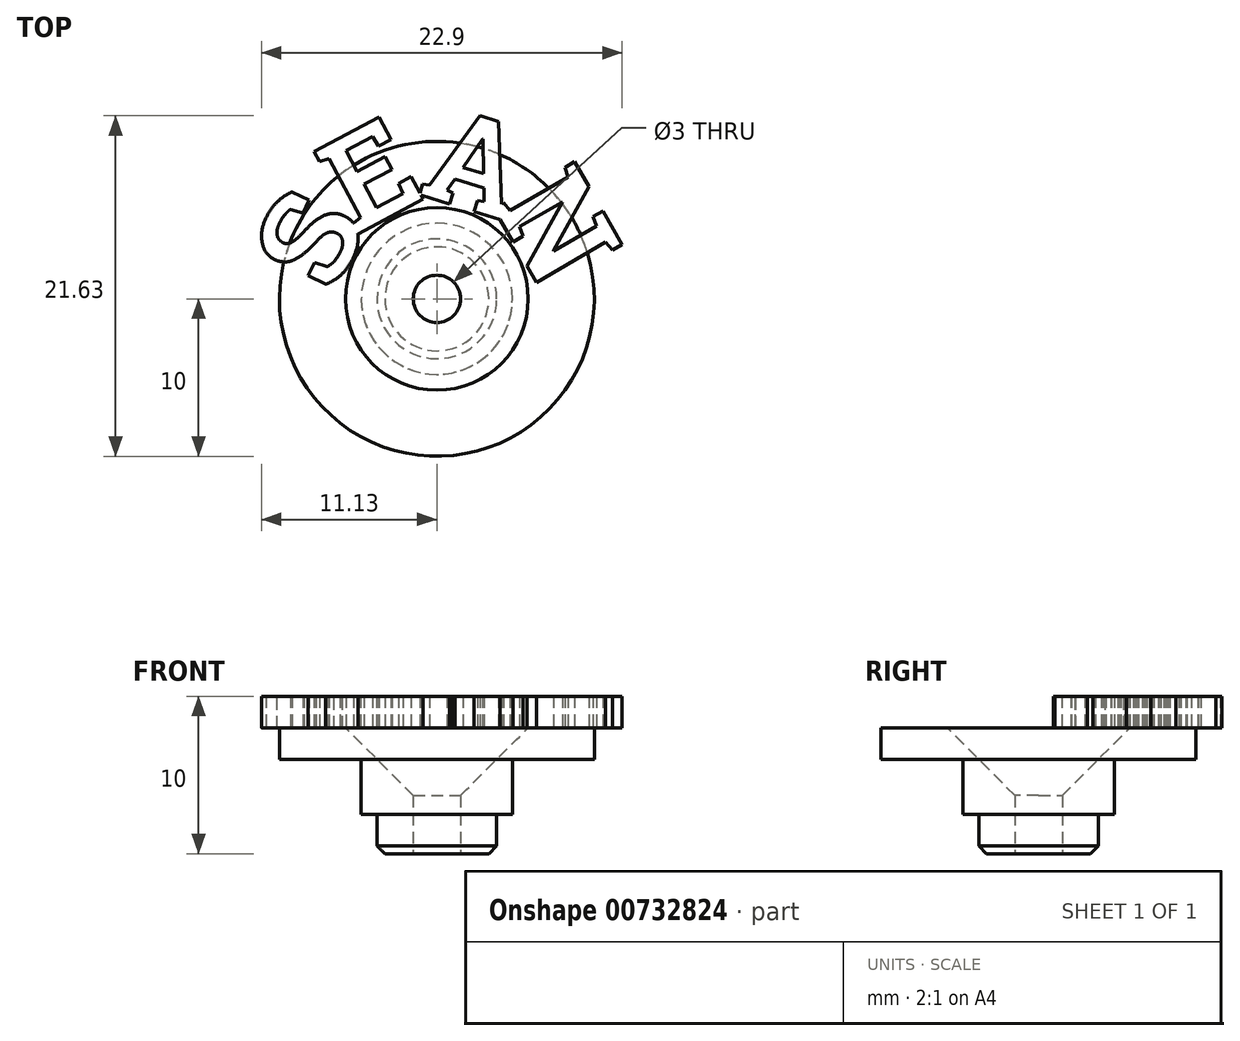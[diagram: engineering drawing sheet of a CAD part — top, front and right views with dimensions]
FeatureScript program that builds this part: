
annotation { "Feature Type Name" : "Feature", "Feature Type Description" : "" }
export const myFeature = defineFeature(function(context is Context, id is Id, definition is map)
    precondition{}
    {
        {
            var Q0;
            Q0=qCreatedBy(makeId("Top.planeOp"),FACE);
            var sketch = newSketch(context, id + "F0", { "sketchPlane" : qUnion([Q0])});
            skCircle(sketch, "E0", {"center": v(0, 0) * mm, "radius": 10 * mm});
            skLineSegment(sketch, "E1", {"start": v(0, 25.77) * mm, "end": v(0, -30.08) * mm, "construction": true});
            skLineSegment(sketch, "E2", {"start": v(23.36, 0) * mm, "end": v(-28.07, 0) * mm, "construction": true});
            skSolve(sketch);
        }
        {
            var Q0;
            Q0=qSketchRegion(id+"F0",true);
            extrude(context, id + "F1", {"entities" : qUnion([Q0]), "depth" : 2 * mm, "offsetDistance" : 25 * mm});
        }
        {
            var Q0;
            Q0=makeQuery(id+"F1.opExtrude","CAP_FACE",FACE,{"disambiguationData":[OSD([sQuery(id+"F0.wireOp",EDGE,"E0")])],"isStart":true});
            var sketch = newSketch(context, id + "F2", { "sketchPlane" : qUnion([Q0])});
            skCircle(sketch, "E3", {"center": v(0, 0) * mm, "radius": 3.8 * mm});
            skSolve(sketch);
        }
        {
            var Q0;
            Q0=qSketchRegion(id+"F2",true);
            extrude(context, id + "F3", {"entities" : qUnion([Q0]), "operationType" : NewBodyOperationType.ADD, "depth" : 6 * mm, "offsetDistance" : 25 * mm});
        }
        {
            var Q0;
            Q0=makeQuery(id+"F3.opExtrude","CAP_EDGE",EDGE,{"disambiguationData":[OSD([sQuery(id+"F2.wireOp",EDGE,"E3")])],"isStart":false});
            chamfer(context, id + "F4", {"entities" : qUnion([Q0]), "width" : .5 * mm, "tangentPropagation" : true});
        }
        {
            var Q0;
            Q0=makeQuery(id+"F3.opExtrude","CAP_FACE",FACE,{"disambiguationData":[OSD([sQuery(id+"F2.wireOp",EDGE,"E3")])],"isStart":false});
            var sketch = newSketch(context, id + "F5", { "sketchPlane" : qUnion([Q0])});
            skCircle(sketch, "E4", {"center": v(0, 0) * mm, "radius": 1.5 * mm});
            skSolve(sketch);
        }
        {
            var Q0;
            Q0=qSketchRegion(id+"F5",true);
            extrude(context, id + "F6", {"entities" : qUnion([Q0]), "operationType" : NewBodyOperationType.REMOVE, "oppositeDirection" : true, "depth" : 25 * mm, "offsetDistance" : 25 * mm});
        }
        {
            var Q0;
            Q0=makeQuery(id+"F1.opExtrude","CAP_FACE",FACE,{"disambiguationData":[OSD([sQuery(id+"F0.wireOp",EDGE,"E0")])],"isStart":true});
            var sketch = newSketch(context, id + "F7", { "sketchPlane" : qUnion([Q0])});
            skCircle(sketch, "E5.0", {"center": v(0, 0) * mm, "radius": 4.8 * mm});
            skCircle(sketch, "E6.0", {"center": v(0, 0) * mm, "radius": 3.8 * mm});
            skSolve(sketch);
        }
        {
            var Q0;
            Q0=qSketchRegion(id+"F7",true);
            extrude(context, id + "F8", {"entities" : qUnion([Q0]), "operationType" : NewBodyOperationType.ADD, "depth" : 3.5 * mm, "offsetDistance" : 25 * mm});
        }
        {
            var Q0;
            Q0=makeQuery(id+"F1.opExtrude","CAP_FACE",FACE,{"disambiguationData":[OSD([sQuery(id+"F0.wireOp",EDGE,"E0")])],"isStart":false});
            var sketch = newSketch(context, id + "F9", { "sketchPlane" : qUnion([Q0])});
            skText(sketch, "E7", { "text": "S", "fontName": "RobotoSlab-Bold.ttf"});
            skText(sketch, "E8", { "text": "E", "fontName": "RobotoSlab-Bold.ttf"});
            skText(sketch, "E9", { "text": "N", "fontName": "RobotoSlab-Bold.ttf"});
            skText(sketch, "E10", { "text": "A", "fontName": "RobotoSlab-Bold.ttf"});
            skLineSegment(sketch, "E11", {"start": v(0, 0) * mm, "end": v(-13.7, 6.68) * mm, "construction": true});
            skLineSegment(sketch, "E12", {"start": v(0, 0) * mm, "end": v(13.74, 7.93) * mm, "construction": true});
            skLineSegment(sketch, "E13", {"start": v(0, 0) * mm, "end": v(4.98, 16.3) * mm, "construction": true});
            skLineSegment(sketch, "E14", {"start": v(0, 0) * mm, "end": v(-7.52, 14.14) * mm, "construction": true});
            skLineSegment(sketch, "E15", {"start": v(0, 0) * mm, "end": v(21.4, 0) * mm, "construction": true});
            const initialGuessF9  = {"E7": [-0.00656, 0.00024, 0.43837, 0.8988, 0.006], "E8": [-0.00521, 0.00402, 0.88295, 0.46947, 0.006], "E9": [0.0035, 0.00594, 0.5, -0.86603, 0.006], "E10": [-0.00127, 0.00666, 0.9563, -0.29237, 0.006]};
            skSetInitialGuess(sketch, initialGuessF9);
            skSolve(sketch);
        }
        {
            var Q0;
            Q0=qSketchRegion(id+"F9",true);
            extrude(context, id + "F10", {"entities" : qUnion([Q0]), "operationType" : NewBodyOperationType.ADD, "depth" : 2 * mm, "offsetDistance" : 25 * mm});
        }
        {
            var Q0;
            Q0=makeQuery(id+"F6.boolean.opBoolean","INTERSECT",EDGE,{"derivedFrom":[makeQuery(id+"F1.opExtrude","CAP_FACE",FACE,{"disambiguationData":[OSD([sQuery(id+"F0.wireOp",EDGE,"E0")])],"isStart":false}),makeQuery(id+"F6.opExtrude","SWEPT_FACE",FACE,{"disambiguationData":[OSD([sQuery(id+"F5.wireOp",EDGE,"E4")])]})]});
            chamfer(context, id + "F11", {"entities" : qUnion([Q0]), "width" : 4.3 * mm, "tangentPropagation" : true});
        }
    });
